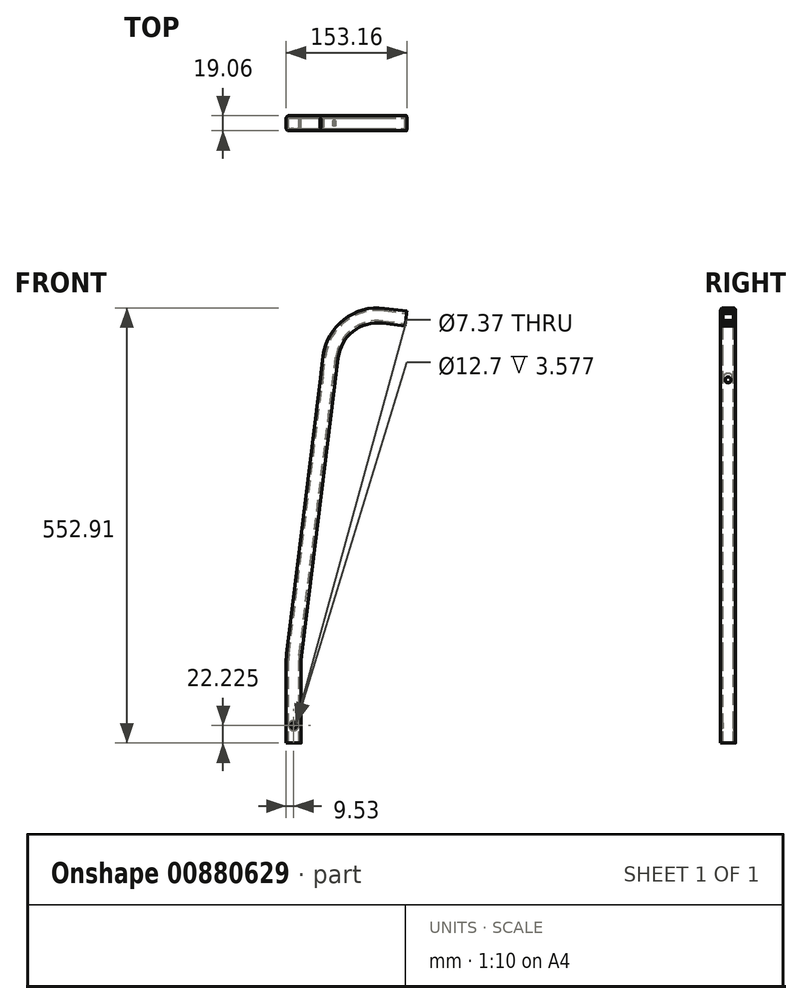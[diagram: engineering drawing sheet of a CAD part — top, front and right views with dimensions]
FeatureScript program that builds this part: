
annotation { "Feature Type Name" : "Feature", "Feature Type Description" : "" }
export const myFeature = defineFeature(function(context is Context, id is Id, definition is map)
    precondition{}
    {
        {
            var Q0;
            Q0=qCreatedBy(makeId("Front.planeOp"),FACE);
            var sketch = newSketch(context, id + "F0", { "sketchPlane" : qUnion([Q0])});
            skLineSegment(sketch, "E0", {"start": v(0, 0) * mm, "end": v(0, 104.9) * mm});
            skLineSegment(sketch, "E1", {"start": v(0.45, 112.25) * mm, "end": v(46.88, 490.41) * mm});
            skLineSegment(sketch, "E2", {"start": v(114.1, 542.94) * mm, "end": v(117.9, 542.47) * mm});
            skArc(sketch, "E3.filletArc", {"start": v(114.1, 542.94) * mm, "mid": v(69.62, 530.6) * mm, "end": v(46.88, 490.41) * mm});
            skPoint(sketch, "E4.visualSharp", {"position": v(0, 108.6) * mm});
            skArc(sketch, "E5.filletArc", {"start": v(0.45, 112.25) * mm, "mid": v(0.11, 108.58) * mm, "end": v(0, 104.9) * mm});
            skSolve(sketch);
        }
        {
            var Q0;
            Q0=qCreatedBy(makeId("Top.planeOp"),FACE);
            var sketch = newSketch(context, id + "F1", { "sketchPlane" : qUnion([Q0])});
            skLineSegment(sketch, "E6.bottom", {"start": v(-6.35, -9.52) * mm, "end": v(6.35, -9.53) * mm});
            skLineSegment(sketch, "E6.top", {"start": v(-6.35, 9.53) * mm, "end": v(6.35, 9.52) * mm});
            skLineSegment(sketch, "E6.left", {"start": v(-9.53, -6.35) * mm, "end": v(-9.52, 6.35) * mm});
            skLineSegment(sketch, "E6.right", {"start": v(9.53, -6.35) * mm, "end": v(9.53, 6.35) * mm});
            skLineSegment(sketch, "E7", {"start": v(0, -9.53) * mm, "end": v(0, 9.53) * mm, "construction": true});
            skPoint(sketch, "E7.startSnap0", {"position": v(0, -9.53) * mm});
            skLineSegment(sketch, "E8", {"start": v(-9.53, 0) * mm, "end": v(9.53, 0) * mm, "construction": true});
            skLineSegment(sketch, "E9.0", {"start": v(-5.46, -6.48) * mm, "end": v(5.46, -6.48) * mm});
            skLineSegment(sketch, "E9.1", {"start": v(-6.48, -5.46) * mm, "end": v(-6.48, 5.46) * mm});
            skLineSegment(sketch, "E9.2", {"start": v(-5.46, 6.48) * mm, "end": v(5.46, 6.48) * mm});
            skLineSegment(sketch, "E9.3", {"start": v(6.48, -5.46) * mm, "end": v(6.48, 5.46) * mm});
            skPoint(sketch, "E10.visualSharp", {"position": v(-6.48, 6.48) * mm});
            skArc(sketch, "E10.filletArc", {"start": v(-5.46, 6.48) * mm, "mid": v(-6.18, 6.18) * mm, "end": v(-6.48, 5.46) * mm});
            skPoint(sketch, "E11.visualSharp", {"position": v(6.48, 6.48) * mm});
            skArc(sketch, "E11.filletArc", {"start": v(6.48, 5.46) * mm, "mid": v(6.18, 6.18) * mm, "end": v(5.46, 6.48) * mm});
            skPoint(sketch, "E12.visualSharp", {"position": v(6.48, -6.48) * mm});
            skArc(sketch, "E12.filletArc", {"start": v(5.46, -6.48) * mm, "mid": v(6.18, -6.18) * mm, "end": v(6.48, -5.46) * mm});
            skPoint(sketch, "E13.visualSharp", {"position": v(-6.48, -6.48) * mm});
            skArc(sketch, "E13.filletArc", {"start": v(-6.48, -5.46) * mm, "mid": v(-6.18, -6.18) * mm, "end": v(-5.46, -6.48) * mm});
            skPoint(sketch, "E14.visualSharp", {"position": v(9.53, -9.53) * mm});
            skArc(sketch, "E14.filletArc", {"start": v(6.35, -9.53) * mm, "mid": v(8.6, -8.6) * mm, "end": v(9.53, -6.35) * mm});
            skPoint(sketch, "E15.visualSharp", {"position": v(-9.53, -9.52) * mm});
            skArc(sketch, "E15.filletArc", {"start": v(-9.52, -6.35) * mm, "mid": v(-8.6, -8.6) * mm, "end": v(-6.35, -9.52) * mm});
            skPoint(sketch, "E16.visualSharp", {"position": v(-9.53, 9.53) * mm});
            skArc(sketch, "E16.filletArc", {"start": v(-6.35, 9.53) * mm, "mid": v(-8.6, 8.6) * mm, "end": v(-9.53, 6.35) * mm});
            skPoint(sketch, "E17.visualSharp", {"position": v(9.53, 9.52) * mm});
            skArc(sketch, "E17.filletArc", {"start": v(9.53, 6.35) * mm, "mid": v(8.6, 8.6) * mm, "end": v(6.35, 9.52) * mm});
            skSolve(sketch);
        }
        {
            var Q0;
            Q0=makeQuery(id+"F1.imprint","IMPRINT",FACE,{"disambiguationData":[TD([[makeQuery(id+"F1.imprint","IMPRINT",EDGE,{"derivedFrom":sQuery(id+"F1.wireOp",EDGE,"uXW7z18t-WP6T-WkQb-FE9L-uBb2vWNNibH4")}),1.0]])]});
            var Q1;
            Q1=makeQuery(id+"F1.imprint","IMPRINT",FACE,{"disambiguationData":[TD([[makeQuery(id+"F1.imprint","IMPRINT",EDGE,{"derivedFrom":sQuery(id+"F1.wireOp",EDGE,"E6.bottom")}),1.0]])]});
            var Q2;
            Q2=sQuery(id+"F0.wireOp",EDGE,"E0");
            var Q3;
            Q3=sQuery(id+"F0.wireOp",EDGE,"E5.filletArc");
            var Q4;
            Q4=sQuery(id+"F0.wireOp",EDGE,"E1");
            var Q5;
            Q5=sQuery(id+"F0.wireOp",EDGE,"E3.filletArc");
            var Q6;
            Q6=sQuery(id+"F0.wireOp",EDGE,"E2");
            sweep(context, id + "F2", {"profiles" : qUnion([Q0, Q1]), "path" : qUnion([Q2, Q3, Q4, Q5, Q6])});
        }
        {
            var Q0;
            Q0=sQuery(id+"F0.wireOp",EDGE,"E2");
            cPlane(context, id + "F3", {"entities" : qUnion([Q0]), "cplaneType" : CPlaneType.LINE_ANGLE, "offset" : 25.4 * mm, "angle" : 90 * degree, "width" : 152.4 * mm, "height" : 152.4 * mm});
        }
        {
            var Q0;
            Q0=qCreatedBy(makeId("Front.planeOp"),FACE);
            var sketch = newSketch(context, id + "F4", { "sketchPlane" : qUnion([Q0])});
            skCircle(sketch, "E18", {"center": v(0, 22.23) * mm, "radius": 3.68 * mm});
            skSolve(sketch);
        }
        {
            var Q0;
            Q0=qSketchRegion(id+"F4",true);
            extrude(context, id + "F5", {"entities" : qUnion([Q0]), "operationType" : NewBodyOperationType.REMOVE, "endBound" : BoundingType.SYMMETRIC, "oppositeDirection" : true, "depth" : 668.02 * mm});
        }
        {
            var Q0;
            Q0=makeQuery(id+"F2.opSweep","SWEPT_FACE",FACE,{"disambiguationData":[OSD([sQuery(id+"F0.wireOp",EDGE,"E1"),sQuery(id+"F1.wireOp",EDGE,"E6.left")])]});
            var sketch = newSketch(context, id + "F6", { "sketchPlane" : qUnion([Q0])});
            skCircle(sketch, "E19", {"center": v(0, 464.53) * mm, "radius": 3.68 * mm});
            skSolve(sketch);
        }
        {
            var Q0;
            Q0=qSketchRegion(id+"F6",true);
            extrude(context, id + "F7", {"entities" : qUnion([Q0]), "operationType" : NewBodyOperationType.REMOVE, "oppositeDirection" : true, "depth" : 25.4 * mm, "offsetDistance" : 25.4 * mm});
        }
        {
            var Q0;
            Q0=makeQuery(id+"F2.opSweep","SWEPT_FACE",FACE,{"disambiguationData":[OSD([sQuery(id+"F0.wireOp",EDGE,"E1"),sQuery(id+"F1.wireOp",EDGE,"E6.left")])]});
            var sketch = newSketch(context, id + "F8", { "sketchPlane" : qUnion([Q0])});
            skCircle(sketch, "E20", {"center": v(0, 464.53) * mm, "radius": 6.35 * mm});
            skSolve(sketch);
        }
        {
            var Q0;
            Q0=qSketchRegion(id+"F8",true);
            extrude(context, id + "F9", {"entities" : qUnion([Q0]), "operationType" : NewBodyOperationType.REMOVE, "oppositeDirection" : true, "depth" : 9.47 * mm, "offsetDistance" : 25.4 * mm});
        }
        {
            var Q0;
            Q0=makeQuery(id+"F2.opSweep","CAP_FACE",FACE,{"disambiguationData":[OSD([sQuery(id+"F0.wireOp",VERTEX,"E2.end"),sQuery(id+"F1.wireOp",EDGE,"E6.bottom"),sQuery(id+"F1.wireOp",EDGE,"E6.top"),sQuery(id+"F1.wireOp",EDGE,"E6.left"),sQuery(id+"F1.wireOp",EDGE,"E6.right"),sQuery(id+"F1.wireOp",EDGE,"E9.0"),sQuery(id+"F1.wireOp",EDGE,"E9.1"),sQuery(id+"F1.wireOp",EDGE,"E9.2"),sQuery(id+"F1.wireOp",EDGE,"E9.3")])],"isStart":false});
            var sketch = newSketch(context, id + "F10", { "sketchPlane" : qUnion([Q0])});
            skLineSegment(sketch, "E21.0", {"start": v(-5.46, 559.27) * mm, "end": v(5.46, 559.27) * mm});
            skArc(sketch, "E21.1", {"start": v(5.46, 559.27) * mm, "mid": v(6.18, 558.98) * mm, "end": v(6.48, 558.26) * mm});
            skLineSegment(sketch, "E21.2", {"start": v(6.48, 558.26) * mm, "end": v(6.48, 547.34) * mm});
            skArc(sketch, "E21.3", {"start": v(6.48, 547.34) * mm, "mid": v(6.18, 546.62) * mm, "end": v(5.46, 546.32) * mm});
            skLineSegment(sketch, "E21.4", {"start": v(5.46, 546.32) * mm, "end": v(-5.46, 546.32) * mm});
            skArc(sketch, "E21.5", {"start": v(-5.46, 546.32) * mm, "mid": v(-6.18, 546.62) * mm, "end": v(-6.48, 547.34) * mm});
            skLineSegment(sketch, "E21.6", {"start": v(-6.48, 547.34) * mm, "end": v(-6.48, 558.26) * mm});
            skArc(sketch, "E21.7", {"start": v(-6.48, 558.26) * mm, "mid": v(-6.18, 558.98) * mm, "end": v(-5.46, 559.27) * mm});
            skLineSegment(sketch, "E22.0", {"start": v(6.35, 562.32) * mm, "end": v(-6.35, 562.32) * mm});
            skArc(sketch, "E22.1", {"start": v(9.53, 559.15) * mm, "mid": v(8.6, 561.4) * mm, "end": v(6.35, 562.32) * mm});
            skLineSegment(sketch, "E22.2", {"start": v(9.53, 559.15) * mm, "end": v(9.52, 546.45) * mm});
            skArc(sketch, "E22.3", {"start": v(6.35, 543.27) * mm, "mid": v(8.6, 544.2) * mm, "end": v(9.53, 546.45) * mm});
            skLineSegment(sketch, "E22.4", {"start": v(-6.35, 543.27) * mm, "end": v(6.35, 543.27) * mm});
            skArc(sketch, "E22.5", {"start": v(-9.53, 546.45) * mm, "mid": v(-8.6, 544.2) * mm, "end": v(-6.35, 543.27) * mm});
            skLineSegment(sketch, "E22.6", {"start": v(-9.52, 559.15) * mm, "end": v(-9.53, 546.45) * mm});
            skArc(sketch, "E22.7", {"start": v(-6.35, 562.32) * mm, "mid": v(-8.6, 561.4) * mm, "end": v(-9.53, 559.15) * mm});
            skSolve(sketch);
        }
        {
            var Q0;
            Q0=qSketchRegion(id+"F10",true);
            extrude(context, id + "F11", {"entities" : qUnion([Q0]), "operationType" : NewBodyOperationType.ADD, "depth" : 24.76 * mm, "offsetDistance" : 25.4 * mm});
        }
        {
            var Q0;
            Q0=makeQuery(id+"F11.boolean.opBoolean","MERGE",FACE,{"derivedFrom":[makeQuery(id+"F2.opSweep","SWEPT_FACE",FACE,{"disambiguationData":[OSD([sQuery(id+"F0.wireOp",EDGE,"E2"),sQuery(id+"F1.wireOp",EDGE,"E6.top")])]}),makeQuery(id+"F11.opExtrude","SWEPT_FACE",FACE,{"disambiguationData":[OSD([sQuery(id+"F10.wireOp",EDGE,"E22.2")])]})]});
            var sketch = newSketch(context, id + "F12", { "sketchPlane" : qUnion([Q0])});
            skCircle(sketch, "E23", {"center": v(0, 22.23) * mm, "radius": 6.35 * mm});
            skSolve(sketch);
        }
        {
            var Q0;
            Q0=qSketchRegion(id+"F12",true);
            extrude(context, id + "F13", {"entities" : qUnion([Q0]), "operationType" : NewBodyOperationType.REMOVE, "oppositeDirection" : true, "depth" : 12.45 * mm, "offsetDistance" : 25.4 * mm});
        }
    });
